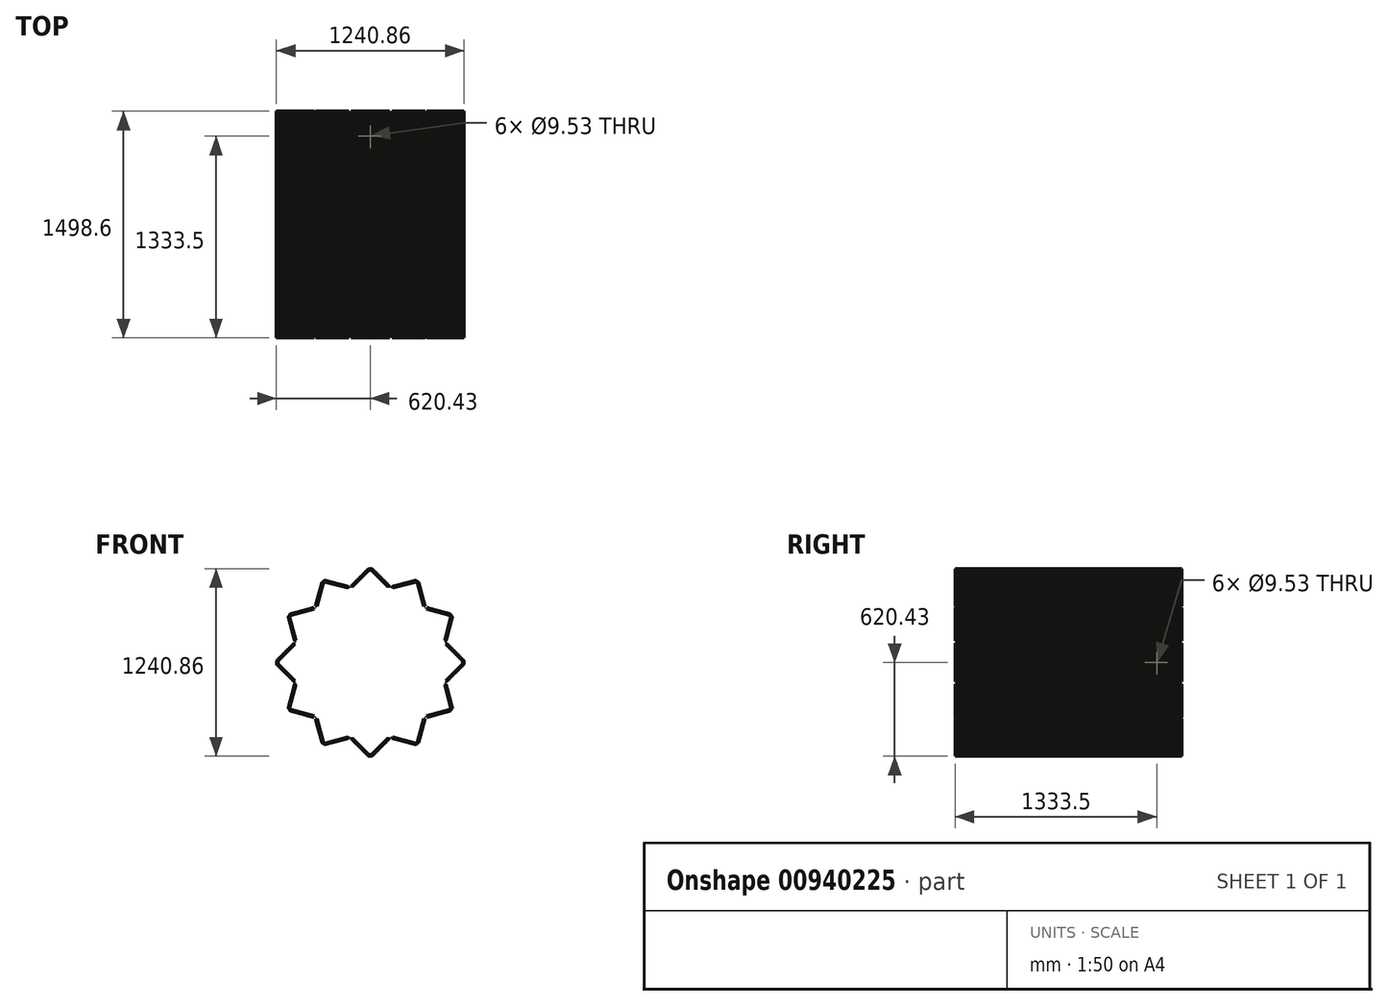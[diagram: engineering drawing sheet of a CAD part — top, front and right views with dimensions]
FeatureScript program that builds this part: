
annotation { "Feature Type Name" : "Feature", "Feature Type Description" : "" }
export const myFeature = defineFeature(function(context is Context, id is Id, definition is map)
    precondition{}
    {
        {
            var Q0;
            Q0=qCreatedBy(makeId("Front.planeOp"),FACE);
            var sketch = newSketch(context, id + "F0", { "sketchPlane" : qUnion([Q0])});
            skLineSegment(sketch, "E0", {"start": v(0, 0) * mm, "end": v(8.21, 0) * mm});
            skLineSegment(sketch, "E1", {"start": v(8.21, 0) * mm, "end": v(119.34, 111.13) * mm});
            skLineSegment(sketch, "E2", {"start": v(119.34, 111.13) * mm, "end": v(123.59, 106.88) * mm});
            skLineSegment(sketch, "E3", {"start": v(123.59, 106.88) * mm, "end": v(10.7, -6) * mm});
            skLineSegment(sketch, "E4", {"start": v(10.7, -6) * mm, "end": v(0, -6) * mm});
            skLineSegment(sketch, "E5", {"start": v(0, -7.02) * mm, "end": v(11.12, -7.02) * mm});
            skLineSegment(sketch, "E6", {"start": v(11.12, -7.02) * mm, "end": v(124.3, 106.16) * mm});
            skLineSegment(sketch, "E7", {"start": v(124.3, 106.16) * mm, "end": v(123.59, 106.88) * mm});
            skLineSegment(sketch, "E8", {"start": v(127, 103.47) * mm, "end": v(124.3, 106.16) * mm});
            skLineSegment(sketch, "E9", {"start": v(8.21, 0) * mm, "end": v(12.7, -10.83) * mm, "construction": true});
            skArc(sketch, "E10", {"start": v(12.7, -10.83) * mm, "mid": v(6.35, -9.65) * mm, "end": v(0, -10.83) * mm});
            skLineSegment(sketch, "E11", {"start": v(0, -10.83) * mm, "end": v(12.7, -10.83) * mm, "construction": true});
            skLineSegment(sketch, "E12", {"start": v(12.7, -10.83) * mm, "end": v(120.46, 96.93) * mm, "construction": true});
            skArc(sketch, "E13.MirrorCS", {"start": v(12.7, -10.83) * mm, "mid": v(16.35, -5.5) * mm, "end": v(21.68, -1.85) * mm});
            skArc(sketch, "E14.1.0.0", {"start": v(21.68, -1.85) * mm, "mid": v(25.33, 3.47) * mm, "end": v(30.66, 7.13) * mm});
            skArc(sketch, "E14.2.0.0", {"start": v(30.66, 7.13) * mm, "mid": v(34.31, 12.45) * mm, "end": v(39.64, 16.1) * mm});
            skLineSegment(sketch, "E14.direction1", {"start": v(12.7, -10.83) * mm, "end": v(21.68, -1.85) * mm, "construction": true});
            skArc(sketch, "E15.0.3.0", {"start": v(39.64, 16.1) * mm, "mid": v(43.3, 21.43) * mm, "end": v(48.62, 25.09) * mm});
            skArc(sketch, "E15.0.4.0", {"start": v(48.62, 25.09) * mm, "mid": v(52.28, 30.41) * mm, "end": v(57.6, 34.07) * mm});
            skArc(sketch, "E15.0.5.0", {"start": v(57.6, 34.07) * mm, "mid": v(61.26, 39.4) * mm, "end": v(66.58, 43.05) * mm});
            skArc(sketch, "E15.0.6.0", {"start": v(66.58, 43.05) * mm, "mid": v(70.24, 48.37) * mm, "end": v(75.56, 52.03) * mm});
            skArc(sketch, "E15.0.7.0", {"start": v(75.56, 52.03) * mm, "mid": v(79.22, 57.35) * mm, "end": v(84.54, 61) * mm});
            skArc(sketch, "E15.0.8.0", {"start": v(84.54, 61) * mm, "mid": v(88.2, 66.34) * mm, "end": v(93.52, 69.99) * mm});
            skArc(sketch, "E15.0.9.0", {"start": v(93.52, 69.99) * mm, "mid": v(97.18, 75.32) * mm, "end": v(102.5, 78.97) * mm});
            skArc(sketch, "E15.0.10.0", {"start": v(102.5, 78.97) * mm, "mid": v(106.16, 84.3) * mm, "end": v(111.48, 87.95) * mm});
            skArc(sketch, "E15.0.11.0", {"start": v(111.48, 87.95) * mm, "mid": v(115.14, 93.28) * mm, "end": v(120.46, 96.93) * mm});
            skArc(sketch, "E15.0.12.0", {"start": v(120.46, 96.93) * mm, "mid": v(122.92, 100.93) * mm, "end": v(126.33, 104.13) * mm});
            skLineSegment(sketch, "E16.trimOffspring", {"start": v(127, 103.47) * mm, "end": v(127, 103.47) * mm, "construction": true});
            skLineSegment(sketch, "E17", {"start": v(0, 0) * mm, "end": v(0, -10.83) * mm, "construction": true});
            skLineSegment(sketch, "E18.MirrorCS", {"start": v(-119.34, 111.13) * mm, "end": v(-123.59, 106.88) * mm});
            skLineSegment(sketch, "E19.MirrorCS", {"start": v(-127, 103.47) * mm, "end": v(-124.3, 106.16) * mm});
            skLineSegment(sketch, "E20.MirrorCS", {"start": v(-124.3, 106.16) * mm, "end": v(-123.59, 106.88) * mm});
            skLineSegment(sketch, "E21.MirrorCS", {"start": v(-8.21, 0) * mm, "end": v(-12.7, -10.83) * mm, "construction": true});
            skLineSegment(sketch, "E22.MirrorCS", {"start": v(0, -10.83) * mm, "end": v(-12.7, -10.83) * mm, "construction": true});
            skArc(sketch, "E23.MirrorCS", {"start": v(-102.5, 78.97) * mm, "mid": v(-106.16, 84.3) * mm, "end": v(-111.48, 87.95) * mm});
            skArc(sketch, "E24.MirrorCS", {"start": v(-120.46, 96.93) * mm, "mid": v(-122.92, 100.93) * mm, "end": v(-126.33, 104.13) * mm});
            skArc(sketch, "E25.MirrorCS", {"start": v(-111.48, 87.95) * mm, "mid": v(-115.14, 93.28) * mm, "end": v(-120.46, 96.93) * mm});
            skLineSegment(sketch, "E26.MirrorCS", {"start": v(-11.12, -7.02) * mm, "end": v(-124.3, 106.16) * mm});
            skArc(sketch, "E27.MirrorCS", {"start": v(-84.54, 61) * mm, "mid": v(-88.2, 66.34) * mm, "end": v(-93.52, 69.99) * mm});
            skArc(sketch, "E28.MirrorCS", {"start": v(-66.58, 43.05) * mm, "mid": v(-70.24, 48.37) * mm, "end": v(-75.56, 52.03) * mm});
            skArc(sketch, "E29.MirrorCS", {"start": v(-75.56, 52.03) * mm, "mid": v(-79.22, 57.35) * mm, "end": v(-84.54, 61) * mm});
            skLineSegment(sketch, "E30.MirrorCS", {"start": v(-123.59, 106.88) * mm, "end": v(-10.7, -6) * mm});
            skLineSegment(sketch, "E31.MirrorCS", {"start": v(0, 0) * mm, "end": v(-8.21, 0) * mm});
            skLineSegment(sketch, "E32.MirrorCS", {"start": v(-10.7, -6) * mm, "end": v(0, -6) * mm});
            skArc(sketch, "E33.MirrorCS", {"start": v(-93.52, 69.99) * mm, "mid": v(-97.18, 75.32) * mm, "end": v(-102.5, 78.97) * mm});
            skArc(sketch, "E34.MirrorCS", {"start": v(-12.7, -10.83) * mm, "mid": v(-16.35, -5.5) * mm, "end": v(-21.68, -1.85) * mm});
            skLineSegment(sketch, "E35.MirrorCS", {"start": v(-12.7, -10.83) * mm, "end": v(-21.68, -1.85) * mm, "construction": true});
            skArc(sketch, "E36.MirrorCS", {"start": v(-21.68, -1.85) * mm, "mid": v(-25.33, 3.47) * mm, "end": v(-30.66, 7.13) * mm});
            skArc(sketch, "E37.MirrorCS", {"start": v(-30.66, 7.13) * mm, "mid": v(-34.31, 12.45) * mm, "end": v(-39.64, 16.1) * mm});
            skArc(sketch, "E38.MirrorCS", {"start": v(-57.6, 34.07) * mm, "mid": v(-61.26, 39.4) * mm, "end": v(-66.58, 43.05) * mm});
            skPoint(sketch, "E39.MirrorP", {"position": v(-127, 103.47) * mm});
            skArc(sketch, "E40.MirrorCS", {"start": v(-39.64, 16.1) * mm, "mid": v(-43.3, 21.43) * mm, "end": v(-48.62, 25.09) * mm});
            skArc(sketch, "E41.MirrorCS", {"start": v(-48.62, 25.09) * mm, "mid": v(-52.28, 30.41) * mm, "end": v(-57.6, 34.07) * mm});
            skLineSegment(sketch, "E42.MirrorCS", {"start": v(0, -7.02) * mm, "end": v(-11.12, -7.02) * mm});
            skLineSegment(sketch, "E43.MirrorCS", {"start": v(-8.21, 0) * mm, "end": v(-119.34, 111.13) * mm});
            skArc(sketch, "E44.MirrorCS", {"start": v(-12.7, -10.83) * mm, "mid": v(-6.35, -9.65) * mm, "end": v(0, -10.83) * mm});
            skLineSegment(sketch, "E45", {"start": v(0, 0) * mm, "end": v(0, 609.6) * mm, "construction": true});
            skPoint(sketch, "E46", {"position": v(0, 609.6) * mm});
            skSolve(sketch);
        }
        {
            var Q0;
            Q0=makeQuery(id+"F0.imprint","IMPRINT",FACE,{"disambiguationData":[TD([[makeQuery(id+"F0.imprint","IMPRINT",EDGE,{"derivedFrom":sQuery(id+"F0.wireOp",EDGE,"E0")}),-1.0]])]});
            var Q1;
            Q1=makeQuery(id+"F0.imprint","IMPRINT",FACE,{"disambiguationData":[TD([[makeQuery(id+"F0.imprint","IMPRINT",EDGE,{"derivedFrom":sQuery(id+"F0.wireOp",EDGE,"E5")}),-1.0]])]});
            var Q2;
            Q2=makeQuery(id+"F0.imprint","IMPRINT",FACE,{"disambiguationData":[TD([[makeQuery(id+"F0.imprint","IMPRINT",EDGE,{"derivedFrom":sQuery(id+"F0.wireOp",EDGE,"E3")}),1.0]])]});
            extrude(context, id + "F1", {"entities" : qUnion([Q0, Q1, Q2]), "depth" : 1498.6 * mm, "offsetDistance" : 25.4 * mm, "symmetric" : true});
        }
        {
            var Q0;
            Q0=makeQuery(id+"F0.imprint","IMPRINT",FACE,{"disambiguationData":[TD([[makeQuery(id+"F0.imprint","IMPRINT",EDGE,{"derivedFrom":sQuery(id+"F0.wireOp",EDGE,"E3")}),1.0]])]});
            extrude(context, id + "F2", {"entities" : qUnion([Q0]), "depth" : 1498.6 * mm, "offsetDistance" : 25.4 * mm, "symmetric" : true});
        }
        {
            var Q0;
            Q0=makeQuery(id+"F0.imprint","IMPRINT",FACE,{"disambiguationData":[TD([[makeQuery(id+"F0.imprint","IMPRINT",EDGE,{"derivedFrom":sQuery(id+"F0.wireOp",EDGE,"E5")}),-1.0]])]});
            extrude(context, id + "F3", {"entities" : qUnion([Q0]), "depth" : 1498.6 * mm, "offsetDistance" : 25.4 * mm, "symmetric" : true});
        }
        {
            var Q0;
            Q0=qCreatedBy(makeId("Top.planeOp"),FACE);
            var sketch = newSketch(context, id + "F4", { "sketchPlane" : qUnion([Q0])});
            skLineSegment(sketch, "E47", {"start": v(0, 374.65) * mm, "end": v(0, -374.65) * mm, "construction": true});
            skPoint(sketch, "E48", {"position": v(0, 0) * mm});
            skCircle(sketch, "E49", {"center": v(0, 584.2) * mm, "radius": 4.76 * mm});
            skLineSegment(sketch, "E50", {"start": v(0, 0) * mm, "end": v(-13.94, 0) * mm, "construction": true});
            skCircle(sketch, "E51.MirrorC", {"center": v(0, -584.2) * mm, "radius": 4.76 * mm});
            skSolve(sketch);
        }
        {
            var Q0;
            Q0=makeQuery(id+"F4.imprint","IMPRINT",FACE,{"disambiguationData":[TD([[makeQuery(id+"F4.imprint","IMPRINT",EDGE,{"derivedFrom":sQuery(id+"F4.wireOp",EDGE,"E49")}),1.0]])]});
            var Q1;
            Q1=makeQuery(id+"F4.imprint","IMPRINT",FACE,{"disambiguationData":[TD([[makeQuery(id+"F4.imprint","IMPRINT",EDGE,{"derivedFrom":sQuery(id+"F4.wireOp",EDGE,"E51.MirrorC")}),-1.0]])]});
            var Q2;
            Q2=sQuery(id+"F4.wireOp",EDGE,"E49");
            var Q3;
            Q3=sQuery(id+"F4.wireOp",EDGE,"E51.MirrorC");
            extrude(context, id + "F5", {"entities" : qUnion([Q0, Q1]), "operationType" : NewBodyOperationType.REMOVE, "surfaceEntities" : qUnion([Q2, Q3]), "endBound" : BoundingType.THROUGH_ALL, "oppositeDirection" : true, "depth" : 96.77 * mm, "offsetDistance" : 25.4 * mm});
        }
        {
            var Q0;
            Q0=qCreatedBy(makeId("Right.planeOp"),FACE);
            var sketch = newSketch(context, id + "F6", { "sketchPlane" : qUnion([Q0])});
            skPoint(sketch, "E52.0", {"position": v(0, 609.6) * mm});
            skLineSegment(sketch, "E53", {"start": v(0, 609.6) * mm, "end": v(352.25, 609.6) * mm});
            skSolve(sketch);
        }
        {
            var Q0;
            Q0=makeQuery(id+"F1.opExtrude","SWEPT_BODY",BODY,{"disambiguationData":[OSD([sQuery(id+"F0.wireOp",EDGE,"E0"),sQuery(id+"F0.wireOp",EDGE,"E1"),sQuery(id+"F0.wireOp",EDGE,"E2"),sQuery(id+"F0.wireOp",EDGE,"E3"),sQuery(id+"F0.wireOp",EDGE,"E4"),sQuery(id+"F0.wireOp",EDGE,"E18.MirrorCS"),sQuery(id+"F0.wireOp",EDGE,"E30.MirrorCS"),sQuery(id+"F0.wireOp",EDGE,"E31.MirrorCS"),sQuery(id+"F0.wireOp",EDGE,"E32.MirrorCS"),sQuery(id+"F0.wireOp",EDGE,"E43.MirrorCS")])]});
            var Q1;
            Q1=makeQuery(id+"F2.opExtrude","SWEPT_BODY",BODY,{"disambiguationData":[OSD([sQuery(id+"F0.wireOp",EDGE,"E3"),sQuery(id+"F0.wireOp",EDGE,"E4"),sQuery(id+"F0.wireOp",EDGE,"E5"),sQuery(id+"F0.wireOp",EDGE,"E6"),sQuery(id+"F0.wireOp",EDGE,"E7"),sQuery(id+"F0.wireOp",EDGE,"E20.MirrorCS"),sQuery(id+"F0.wireOp",EDGE,"E26.MirrorCS"),sQuery(id+"F0.wireOp",EDGE,"E30.MirrorCS"),sQuery(id+"F0.wireOp",EDGE,"E32.MirrorCS"),sQuery(id+"F0.wireOp",EDGE,"E42.MirrorCS")])]});
            var Q2;
            Q2=makeQuery(id+"F3.opExtrude","SWEPT_BODY",BODY,{"disambiguationData":[OSD([sQuery(id+"F0.wireOp",EDGE,"E5"),sQuery(id+"F0.wireOp",EDGE,"E6"),sQuery(id+"F0.wireOp",EDGE,"E8"),sQuery(id+"F0.wireOp",EDGE,"E10"),sQuery(id+"F0.wireOp",EDGE,"E13.MirrorCS"),sQuery(id+"F0.wireOp",EDGE,"E14.1.0.0"),sQuery(id+"F0.wireOp",EDGE,"E14.2.0.0"),sQuery(id+"F0.wireOp",EDGE,"E15.0.3.0"),sQuery(id+"F0.wireOp",EDGE,"E15.0.4.0"),sQuery(id+"F0.wireOp",EDGE,"E15.0.5.0"),sQuery(id+"F0.wireOp",EDGE,"E15.0.6.0"),sQuery(id+"F0.wireOp",EDGE,"E15.0.7.0"),sQuery(id+"F0.wireOp",EDGE,"E15.0.8.0"),sQuery(id+"F0.wireOp",EDGE,"E15.0.9.0"),sQuery(id+"F0.wireOp",EDGE,"E15.0.10.0"),sQuery(id+"F0.wireOp",EDGE,"E15.0.11.0"),sQuery(id+"F0.wireOp",EDGE,"E15.0.12.0"),sQuery(id+"F0.wireOp",EDGE,"E19.MirrorCS"),sQuery(id+"F0.wireOp",EDGE,"E23.MirrorCS"),sQuery(id+"F0.wireOp",EDGE,"E24.MirrorCS"),sQuery(id+"F0.wireOp",EDGE,"E25.MirrorCS"),sQuery(id+"F0.wireOp",EDGE,"E26.MirrorCS"),sQuery(id+"F0.wireOp",EDGE,"E27.MirrorCS"),sQuery(id+"F0.wireOp",EDGE,"E28.MirrorCS"),sQuery(id+"F0.wireOp",EDGE,"E29.MirrorCS"),sQuery(id+"F0.wireOp",EDGE,"E33.MirrorCS"),sQuery(id+"F0.wireOp",EDGE,"E34.MirrorCS"),sQuery(id+"F0.wireOp",EDGE,"E36.MirrorCS"),sQuery(id+"F0.wireOp",EDGE,"E37.MirrorCS"),sQuery(id+"F0.wireOp",EDGE,"E38.MirrorCS"),sQuery(id+"F0.wireOp",EDGE,"E40.MirrorCS"),sQuery(id+"F0.wireOp",EDGE,"E41.MirrorCS"),sQuery(id+"F0.wireOp",EDGE,"E42.MirrorCS"),sQuery(id+"F0.wireOp",EDGE,"E44.MirrorCS")])]});
            var Q3;
            Q3=sQuery(id+"F6.wireOp",EDGE,"E53");
            circularPattern(context, id + "F7", {"entities" : qUnion([Q0, Q1, Q2]), "axis" : qUnion([Q3]), "angle" : 360 * degree, "instanceCount" : 12, "equalSpace" : true});
        }
    });
